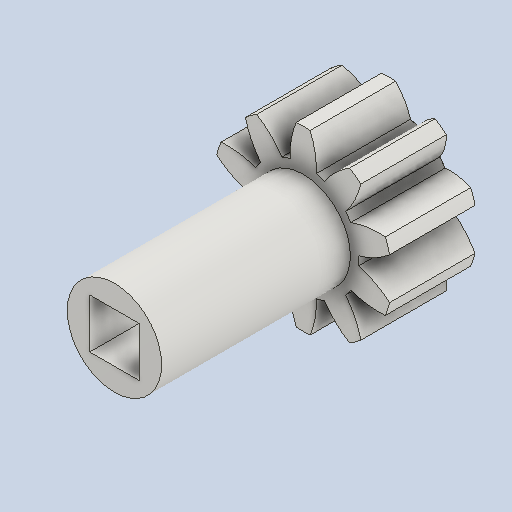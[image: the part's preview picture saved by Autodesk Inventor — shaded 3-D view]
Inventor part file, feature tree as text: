
AUTODESK INVENTOR PART (.ipt)
format: ipt  version: 2022 (Build 260153000, 153)  size: 269,824 bytes
history: native  units: in
note: dims shown in document units (in); Inventor stores cm internally (conversion verified against a paired STEP export)
features: other x12, sketch x6, plane x3
ambient origin geometry x8: Origin, YZ Plane, XZ Plane, XY Plane, X Axis, Y Axis, Z Axis, Center Point
bodies: Solid1 (feature_tree)
feature tree (21):
  other  "Spur Gear1"
  other  "Solid1::Spur Gear1"
  other  "TaggingFeature1"
  sketch  "Sketch1"  dims[d0=0.3937in]
  sketch  "Sketch2"  dims[d9=0.0in]
  sketch  "Sketch3"  dims[d14=0.0in]
  sketch  "Sketch4"  dims[d15=0.9352in]
  sketch  "Sketch5"  dims[d16=0.0in]
  sketch  "Sketch6"  dims[d17=0.0in d18=0.0in d19=0.9352in]
  plane  "XZ Plane_1"
  plane  "Work Plane2"
  plane  "Work Plane3"
  other  "Srf1"
  other  "Srf1::Derived"
  other  "Start plane iMate"
  other  "Distance iMate"
  other  "Position iMate"
  other  "Mesh iMate"
  other  "Axis iMate"
  other  "Mesh iMate2"
  other  "Align iMate"
